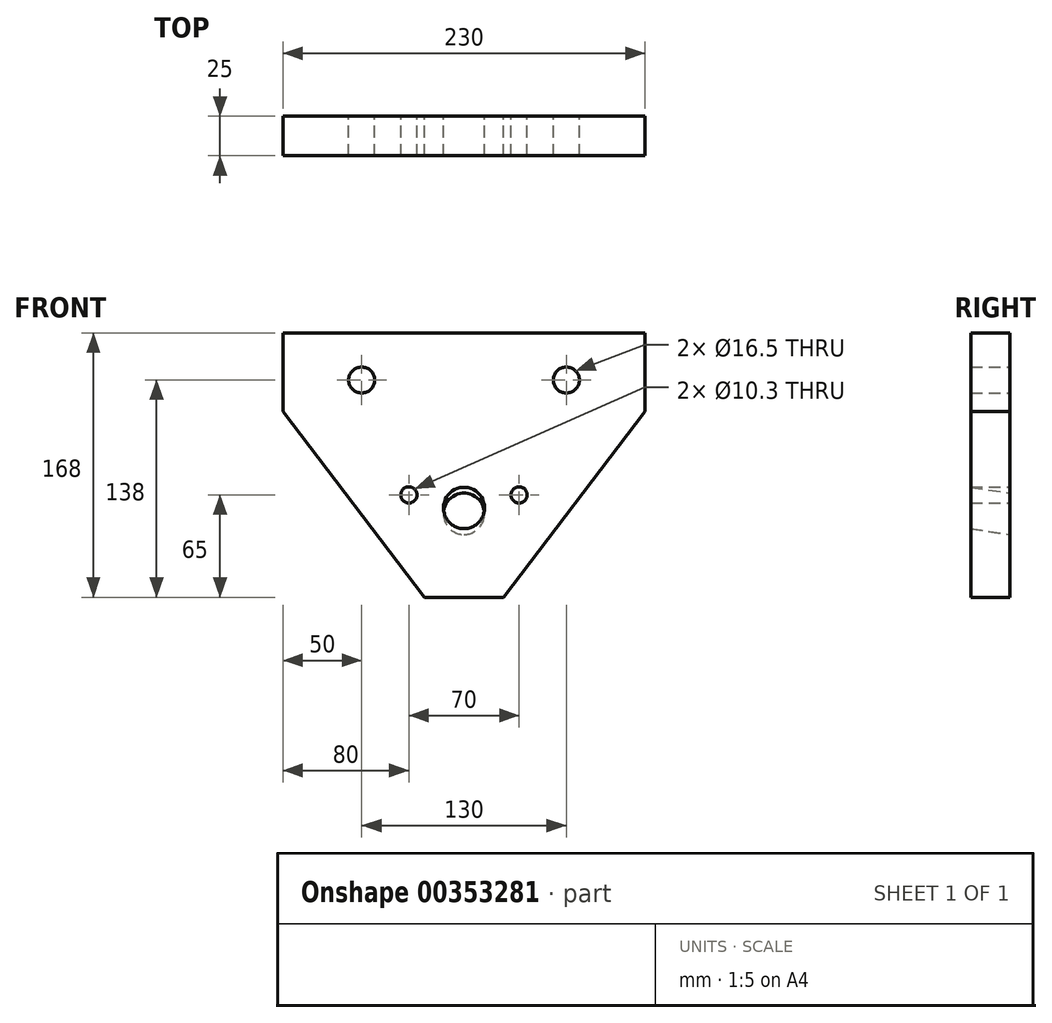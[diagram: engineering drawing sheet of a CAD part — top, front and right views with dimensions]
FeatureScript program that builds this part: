
annotation { "Feature Type Name" : "Feature", "Feature Type Description" : "" }
export const myFeature = defineFeature(function(context is Context, id is Id, definition is map)
    precondition{}
    {
        {
            var Q0;
            Q0=qCreatedBy(makeId("Front.planeOp"),FACE);
            var sketch = newSketch(context, id + "F0", { "sketchPlane" : qUnion([Q0])});
            skCircle(sketch, "E0", {"center": v(0, 0) * mm, "radius": 13 * mm});
            skCircle(sketch, "E1", {"center": v(-35, 12) * mm, "radius": 5.15 * mm});
            skCircle(sketch, "E2.MirrorC", {"center": v(35, 12) * mm, "radius": 5.15 * mm});
            skLineSegment(sketch, "E3", {"start": v(-25, -53) * mm, "end": v(25, -53) * mm});
            skLineSegment(sketch, "E4", {"start": v(25, -53) * mm, "end": v(115, 65) * mm});
            skLineSegment(sketch, "E5", {"start": v(115, 65) * mm, "end": v(115, 115) * mm});
            skLineSegment(sketch, "E6.MirrorCS", {"start": v(-115, 65) * mm, "end": v(-115, 115) * mm});
            skLineSegment(sketch, "E7.MirrorCS", {"start": v(-25, -53) * mm, "end": v(-115, 65) * mm});
            skPoint(sketch, "E8.orphan", {"position": v(88.04, 93.92) * mm});
            skPoint(sketch, "E9.MirrorCS.start.orphan", {"position": v(-115, 115) * mm});
            skPoint(sketch, "E10.orphan", {"position": v(-88.04, 93.92) * mm});
            skLineSegment(sketch, "E11", {"start": v(115, 115) * mm, "end": v(-115, 115) * mm});
            skCircle(sketch, "E12", {"center": v(-65, 85) * mm, "radius": 8.25 * mm});
            skPoint(sketch, "E13.end.orphan", {"position": v(115, -41.66) * mm});
            skCircle(sketch, "E14.MirrorC", {"center": v(65, 85) * mm, "radius": 8.25 * mm});
            skSolve(sketch);
        }
        {
            var Q0;
            Q0=makeQuery(id+"F0.imprint","IMPRINT",FACE,{"disambiguationData":[TD([[makeQuery(id+"F0.imprint","IMPRINT",EDGE,{"derivedFrom":sQuery(id+"F0.wireOp",EDGE,"E0")}),-1.0]])]});
            var Q1;
            Q1=makeQuery(id+"F0.imprint","IMPRINT",FACE,{"disambiguationData":[TD([[makeQuery(id+"F0.imprint","IMPRINT",EDGE,{"derivedFrom":sQuery(id+"F0.wireOp",EDGE,"E0")}),1.0]])]});
            extrude(context, id + "F1", {"entities" : qUnion([Q0, Q1]), "depth" : 25 * mm});
        }
        {
            var Q0;
            Q0=qCreatedBy(makeId("Right.planeOp"),FACE);
            var sketch = newSketch(context, id + "F2", { "sketchPlane" : qUnion([Q0])});
            skCircle(sketch, "E15", {"center": v(0, 0) * mm, "radius": 13 * mm});
            skSolve(sketch);
        }
        {
            var Q0;
            Q0=sQuery(id+"F2.wireOp",EDGE,"E15");
            var Q1;
            Q1=sQuery(id+"F0.wireOp",EDGE,"E0");
            cPlane(context, id + "F3", {"entities" : qUnion([Q0, Q1]), "cplaneType" : CPlaneType.LINE_ANGLE, "offset" : 25 * mm, "angle" : 98.5 * degree, "oppositeDirection" : true, "width" : 150 * mm, "height" : 150 * mm});
        }
        {
            var Q0;
            Q0=qCreatedBy(id+"F3.planeOp",FACE);
            var sketch = newSketch(context, id + "F4", { "sketchPlane" : qUnion([Q0])});
            skCircle(sketch, "E16", {"center": v(0, 0) * mm, "radius": 13 * mm});
            skSolve(sketch);
        }
        {
            var Q0;
            Q0=makeQuery(id+"F4.imprint","IMPRINT",FACE,{"disambiguationData":[TD([[makeQuery(id+"F4.imprint","IMPRINT",EDGE,{"derivedFrom":sQuery(id+"F4.wireOp",EDGE,"E16")}),1.0]])]});
            extrude(context, id + "F5", {"entities" : qUnion([Q0]), "operationType" : NewBodyOperationType.REMOVE, "endBound" : BoundingType.SYMMETRIC, "depth" : 100 * mm});
        }
    });
